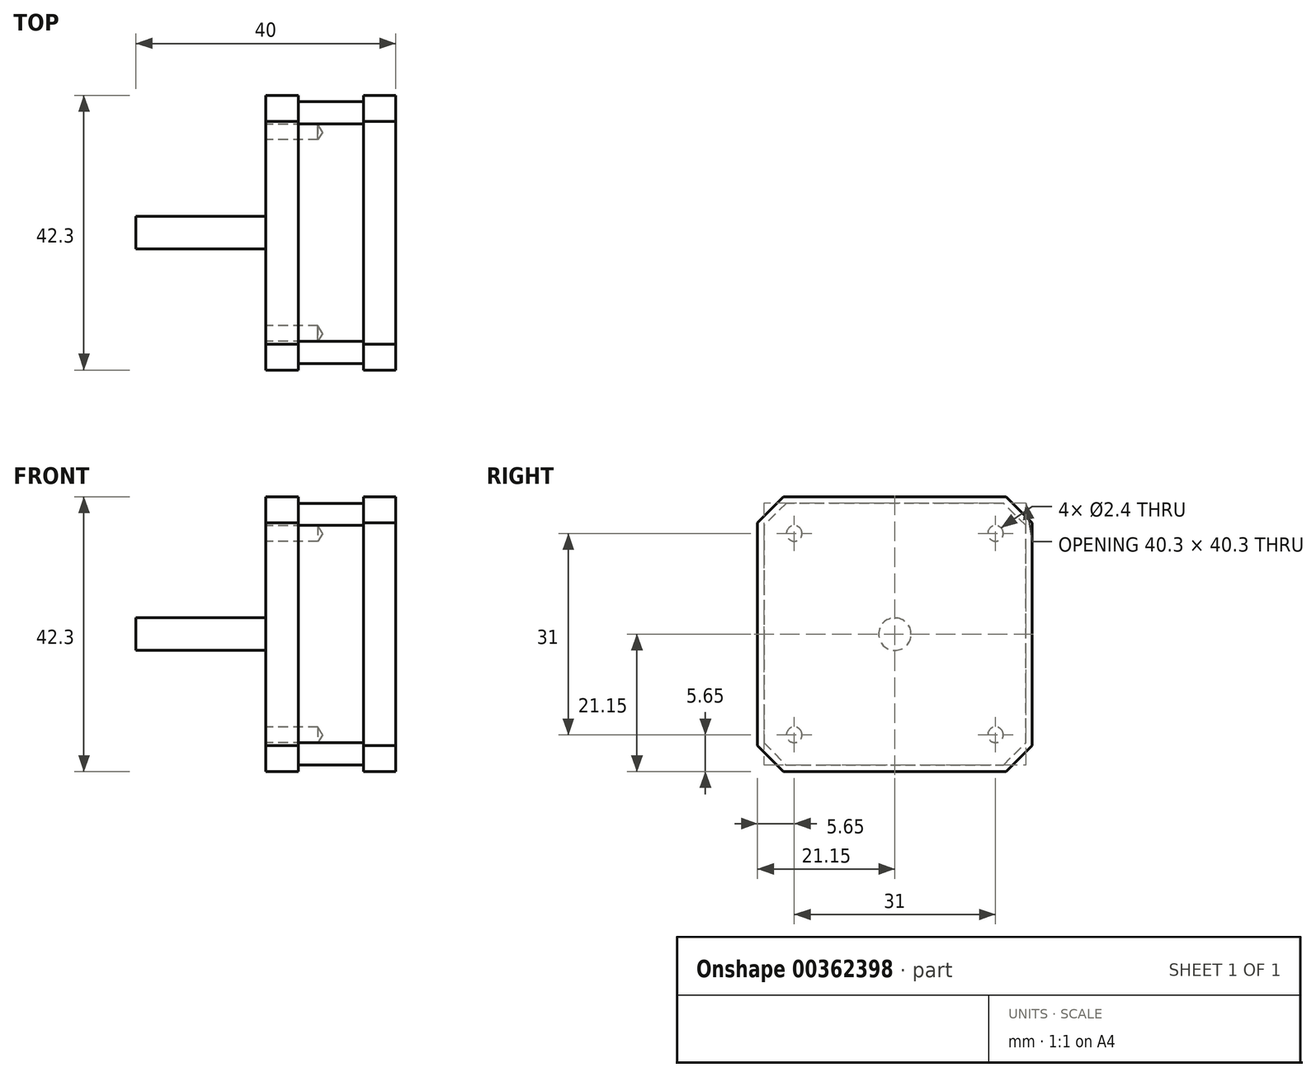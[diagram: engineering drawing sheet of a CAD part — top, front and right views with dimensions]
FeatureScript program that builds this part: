
annotation { "Feature Type Name" : "Feature", "Feature Type Description" : "" }
export const myFeature = defineFeature(function(context is Context, id is Id, definition is map)
    precondition{}
    {
        {
            var Q0;
            Q0=qCreatedBy(makeId("Right.planeOp"),FACE);
            var sketch = newSketch(context, id + "F0", { "sketchPlane" : qUnion([Q0])});
            skLineSegment(sketch, "E0.bottom", {"start": v(21.15, -21.15) * mm, "end": v(-21.15, -21.15) * mm});
            skLineSegment(sketch, "E0.top", {"start": v(21.15, 21.15) * mm, "end": v(-21.15, 21.15) * mm});
            skLineSegment(sketch, "E0.left", {"start": v(21.15, -21.15) * mm, "end": v(21.15, 21.15) * mm});
            skLineSegment(sketch, "E0.right", {"start": v(-21.15, -21.15) * mm, "end": v(-21.15, 21.15) * mm});
            skPoint(sketch, "E0.middle", {"position": v(0, 0) * mm});
            skSolve(sketch);
        }
        {
            var Q0;
            Q0=qSketchRegion(id+"F0",true);
            extrude(context, id + "F1", {"entities" : qUnion([Q0]), "endBound" : BoundingType.SYMMETRIC, "depth" : 20 * mm});
        }
        {
            var Q0;
            Q0=makeQuery(id+"F1.opExtrude","SWEPT_EDGE",EDGE,{"disambiguationData":[OSD([sQuery(id+"F0.wireOp",EDGE,"E0.top"),sQuery(id+"F0.wireOp",EDGE,"E0.right")])]});
            var Q1;
            Q1=makeQuery(id+"F1.opExtrude","SWEPT_EDGE",EDGE,{"disambiguationData":[OSD([sQuery(id+"F0.wireOp",EDGE,"E0.top"),sQuery(id+"F0.wireOp",EDGE,"E0.left")])]});
            var Q2;
            Q2=makeQuery(id+"F1.opExtrude","SWEPT_EDGE",EDGE,{"disambiguationData":[OSD([sQuery(id+"F0.wireOp",EDGE,"E0.bottom"),sQuery(id+"F0.wireOp",EDGE,"E0.right")])]});
            var Q3;
            Q3=makeQuery(id+"F1.opExtrude","SWEPT_EDGE",EDGE,{"disambiguationData":[OSD([sQuery(id+"F0.wireOp",EDGE,"E0.bottom"),sQuery(id+"F0.wireOp",EDGE,"E0.left")])]});
            chamfer(context, id + "F2", {"entities" : qUnion([Q0, Q1, Q2, Q3]), "width" : 4 * mm, "tangentPropagation" : true});
        }
        {
            var Q0;
            Q0=qCreatedBy(makeId("Right.planeOp"),FACE);
            var sketch = newSketch(context, id + "F3", { "sketchPlane" : qUnion([Q0])});
            skLineSegment(sketch, "E1.0", {"start": v(-20.15, -16.74) * mm, "end": v(-16.74, -20.15) * mm});
            skLineSegment(sketch, "E1.1", {"start": v(-20.15, 16.74) * mm, "end": v(-20.15, -16.74) * mm});
            skLineSegment(sketch, "E1.2", {"start": v(-16.74, -20.15) * mm, "end": v(16.74, -20.15) * mm});
            skLineSegment(sketch, "E1.3", {"start": v(-16.74, 20.15) * mm, "end": v(-20.15, 16.74) * mm});
            skLineSegment(sketch, "E1.4", {"start": v(16.74, -20.15) * mm, "end": v(20.15, -16.74) * mm});
            skLineSegment(sketch, "E1.5", {"start": v(20.15, -16.74) * mm, "end": v(20.15, 16.74) * mm});
            skLineSegment(sketch, "E1.6", {"start": v(20.15, 16.74) * mm, "end": v(16.74, 20.15) * mm});
            skLineSegment(sketch, "E1.7", {"start": v(16.74, 20.15) * mm, "end": v(-16.74, 20.15) * mm});
            skLineSegment(sketch, "E2.bottom", {"start": v(21.5, -21.5) * mm, "end": v(-21.5, -21.5) * mm});
            skLineSegment(sketch, "E2.top", {"start": v(21.5, 21.5) * mm, "end": v(-21.5, 21.5) * mm});
            skLineSegment(sketch, "E2.left", {"start": v(21.5, -21.5) * mm, "end": v(21.5, 21.5) * mm});
            skLineSegment(sketch, "E2.right", {"start": v(-21.5, -21.5) * mm, "end": v(-21.5, 21.5) * mm});
            skPoint(sketch, "E2.middle", {"position": v(0, 0) * mm});
            skSolve(sketch);
        }
        {
            var Q0;
            Q0=qSketchRegion(id+"F3",true);
            extrude(context, id + "F4", {"entities" : qUnion([Q0]), "operationType" : NewBodyOperationType.REMOVE, "endBound" : BoundingType.SYMMETRIC, "oppositeDirection" : true, "depth" : 10 * mm});
        }
        {
            var Q0;
            Q0=makeQuery(id+"F1.opExtrude","CAP_FACE",FACE,{"disambiguationData":[OSD([sQuery(id+"F0.wireOp",EDGE,"E0.bottom"),sQuery(id+"F0.wireOp",EDGE,"E0.top"),sQuery(id+"F0.wireOp",EDGE,"E0.left"),sQuery(id+"F0.wireOp",EDGE,"E0.right")])],"isStart":true});
            var sketch = newSketch(context, id + "F5", { "sketchPlane" : qUnion([Q0])});
            skCircle(sketch, "E3", {"center": v(0, 0) * mm, "radius": 2.5 * mm});
            skSolve(sketch);
        }
        {
            var Q0;
            Q0=qSketchRegion(id+"F5",true);
            extrude(context, id + "F6", {"entities" : qUnion([Q0]), "operationType" : NewBodyOperationType.ADD, "depth" : 20 * mm});
        }
        {
            var Q0;
            Q0=makeQuery(id+"F1.opExtrude","CAP_FACE",FACE,{"disambiguationData":[OSD([sQuery(id+"F0.wireOp",EDGE,"E0.bottom"),sQuery(id+"F0.wireOp",EDGE,"E0.top"),sQuery(id+"F0.wireOp",EDGE,"E0.left"),sQuery(id+"F0.wireOp",EDGE,"E0.right")])],"isStart":true});
            var sketch = newSketch(context, id + "F7", { "sketchPlane" : qUnion([Q0])});
            skPoint(sketch, "E4", {"position": v(-15.5, 15.5) * mm});
            skPoint(sketch, "E5.0.1.0", {"position": v(-15.5, -15.5) * mm});
            skPoint(sketch, "E5.1.0.0", {"position": v(15.5, 15.5) * mm});
            skPoint(sketch, "E5.1.1.0", {"position": v(15.5, -15.5) * mm});
            skLineSegment(sketch, "E5.direction1", {"start": v(-15.5, 15.5) * mm, "end": v(15.5, 15.5) * mm, "construction": true});
            skLineSegment(sketch, "E5.direction2", {"start": v(-15.5, 15.5) * mm, "end": v(-15.5, -15.5) * mm, "construction": true});
            skSolve(sketch);
        }
        {
            var Q0;
            Q0=sQuery(id+"F7.wireOp",VERTEX,"E4");
            var Q1;
            Q1=sQuery(id+"F7.wireOp",VERTEX,"E5.1.0.0");
            var Q2;
            Q2=sQuery(id+"F7.wireOp",VERTEX,"E5.0.1.0");
            var Q3;
            Q3=sQuery(id+"F7.wireOp",VERTEX,"E5.1.1.0");
            var Q4;
            Q4=makeQuery(id+"F1.opExtrude","SWEPT_BODY",BODY,{"disambiguationData":[OSD([sQuery(id+"F0.wireOp",EDGE,"E0.bottom"),sQuery(id+"F0.wireOp",EDGE,"E0.top"),sQuery(id+"F0.wireOp",EDGE,"E0.left"),sQuery(id+"F0.wireOp",EDGE,"E0.right")])]});
            hole(context, id + "F8", {"style" : HoleStyle.SIMPLE, "endStyle" : HoleEndStyle.BLIND, "standardTappedOrClearance" : lookupTablePath({ "standard" : "ISO", "engagement" : "75%", "pitch" : "0.6 mm", "size" : "M3", "type" : "Tapped" }), "standardBlindInLast" : lookupTablePath({ "standard" : "ISO", "engagement" : "75%", "pitch" : "0.6 mm", "size" : "M3", "type" : "Tapped" }), "holeDiameter" : 2.4 * mm, "holeDepth" : 8 * mm, "locations" : qUnion([Q0, Q1, Q2, Q3]), "scope" : qUnion([Q4])});
        }
    });
